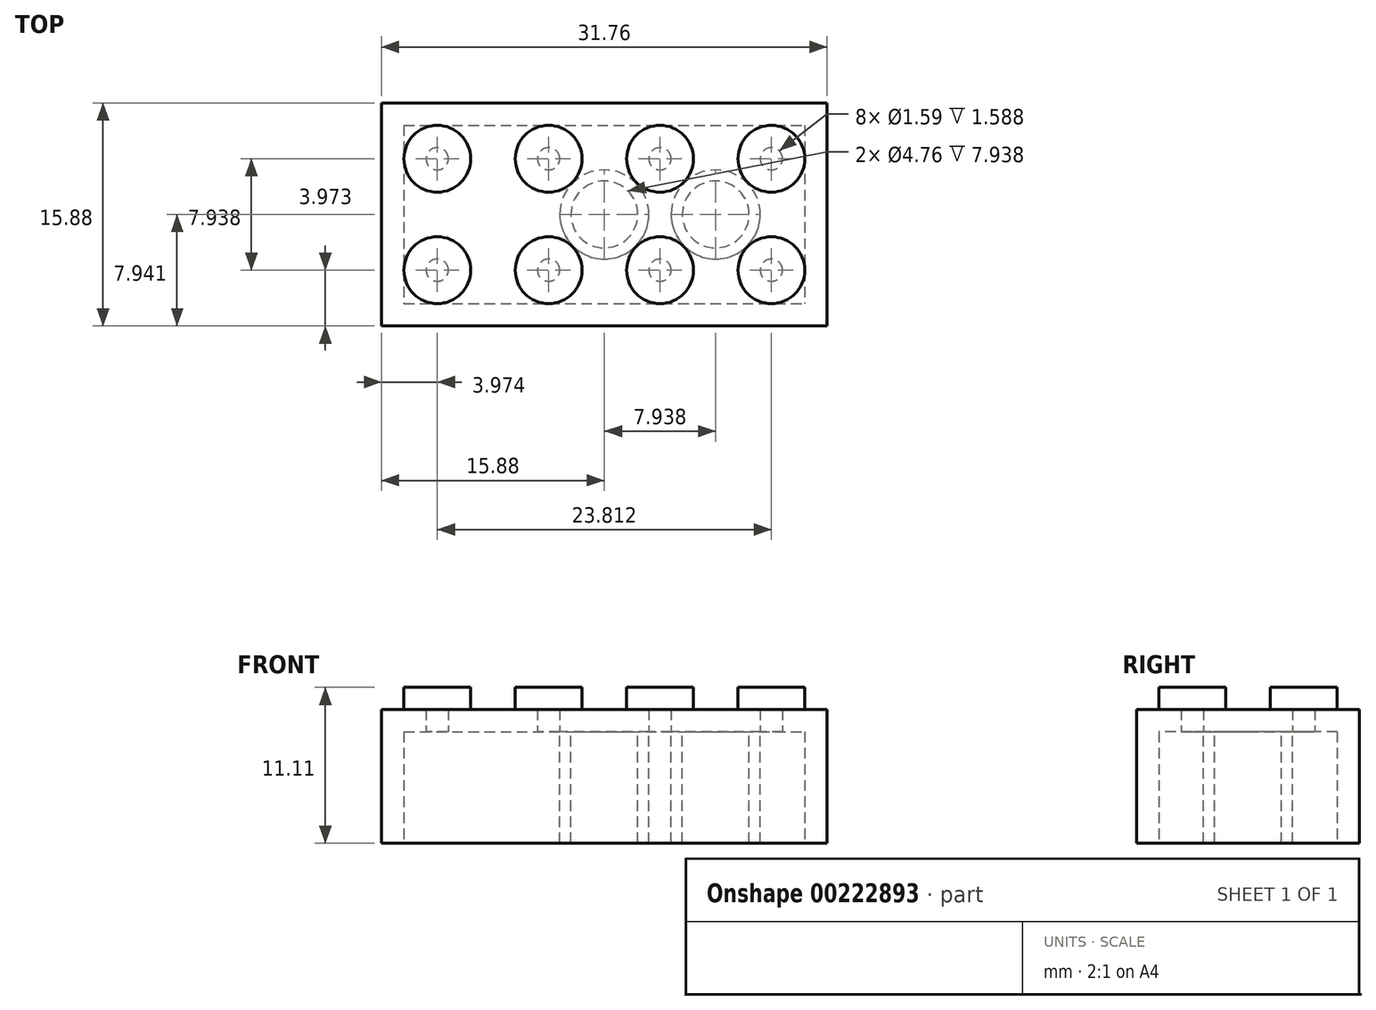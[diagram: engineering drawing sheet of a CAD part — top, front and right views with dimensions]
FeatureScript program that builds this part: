
annotation { "Feature Type Name" : "Feature", "Feature Type Description" : "" }
export const myFeature = defineFeature(function(context is Context, id is Id, definition is map)
    precondition{}
    {
        {
            var Q0;
            Q0=qCreatedBy(makeId("Top.planeOp"),FACE);
            var sketch = newSketch(context, id + "F0", { "sketchPlane" : qUnion([Q0])});
            skLineSegment(sketch, "E0.bottom", {"start": v(-15.88, 3.97) * mm, "end": v(15.87, 3.97) * mm});
            skLineSegment(sketch, "E0.top", {"start": v(-15.88, -11.9) * mm, "end": v(15.87, -11.9) * mm});
            skLineSegment(sketch, "E0.left", {"start": v(-15.88, 3.97) * mm, "end": v(-15.88, -11.9) * mm});
            skLineSegment(sketch, "E0.right", {"start": v(15.88, 3.97) * mm, "end": v(15.88, -11.9) * mm});
            skCircle(sketch, "E1", {"center": v(-11.9, 0) * mm, "radius": 2.38 * mm});
            skCircle(sketch, "E2.0.1.0", {"center": v(-11.9, -7.94) * mm, "radius": 2.38 * mm});
            skCircle(sketch, "E2.1.0.0", {"center": v(-3.97, 0) * mm, "radius": 2.38 * mm});
            skCircle(sketch, "E2.1.1.0", {"center": v(-3.97, -7.94) * mm, "radius": 2.38 * mm});
            skCircle(sketch, "E2.2.0.0", {"center": v(3.97, 0) * mm, "radius": 2.38 * mm});
            skCircle(sketch, "E2.2.1.0", {"center": v(3.97, -7.94) * mm, "radius": 2.38 * mm});
            skCircle(sketch, "E2.3.0.0", {"center": v(11.9, 0) * mm, "radius": 2.38 * mm});
            skCircle(sketch, "E2.3.1.0", {"center": v(11.9, -7.94) * mm, "radius": 2.38 * mm});
            skLineSegment(sketch, "E2.direction1", {"start": v(-11.9, 0) * mm, "end": v(-3.97, 0) * mm, "construction": true});
            skLineSegment(sketch, "E2.direction2", {"start": v(-11.9, 0) * mm, "end": v(-11.9, -7.94) * mm, "construction": true});
            skSolve(sketch);
        }
        {
            var Q0;
            Q0=makeQuery(id+"F0.imprint","IMPRINT",FACE,{"disambiguationData":[TD([[makeQuery(id+"F0.imprint","IMPRINT",EDGE,{"derivedFrom":sQuery(id+"F0.wireOp",EDGE,"E0.bottom")}),-1.0]])]});
            extrude(context, id + "F1", {"entities" : qUnion([Q0]), "depth" : 9.52 * mm});
        }
        {
            var Q0;
            Q0=makeQuery(id+"F0.imprint","IMPRINT",FACE,{"disambiguationData":[TD([[makeQuery(id+"F0.imprint","IMPRINT",EDGE,{"derivedFrom":sQuery(id+"F0.wireOp",EDGE,"E1")}),1.0]])]});
            var Q1;
            Q1=makeQuery(id+"F0.imprint","IMPRINT",FACE,{"disambiguationData":[TD([[makeQuery(id+"F0.imprint","IMPRINT",EDGE,{"derivedFrom":sQuery(id+"F0.wireOp",EDGE,"E2.0.1.0")}),1.0]])]});
            var Q2;
            Q2=makeQuery(id+"F0.imprint","IMPRINT",FACE,{"disambiguationData":[TD([[makeQuery(id+"F0.imprint","IMPRINT",EDGE,{"derivedFrom":sQuery(id+"F0.wireOp",EDGE,"E2.1.1.0")}),1.0]])]});
            var Q3;
            Q3=makeQuery(id+"F0.imprint","IMPRINT",FACE,{"disambiguationData":[TD([[makeQuery(id+"F0.imprint","IMPRINT",EDGE,{"derivedFrom":sQuery(id+"F0.wireOp",EDGE,"E2.1.0.0")}),1.0]])]});
            var Q4;
            Q4=makeQuery(id+"F0.imprint","IMPRINT",FACE,{"disambiguationData":[TD([[makeQuery(id+"F0.imprint","IMPRINT",EDGE,{"derivedFrom":sQuery(id+"F0.wireOp",EDGE,"E2.2.0.0")}),1.0]])]});
            var Q5;
            Q5=makeQuery(id+"F0.imprint","IMPRINT",FACE,{"disambiguationData":[TD([[makeQuery(id+"F0.imprint","IMPRINT",EDGE,{"derivedFrom":sQuery(id+"F0.wireOp",EDGE,"E2.2.1.0")}),1.0]])]});
            var Q6;
            Q6=makeQuery(id+"F0.imprint","IMPRINT",FACE,{"disambiguationData":[TD([[makeQuery(id+"F0.imprint","IMPRINT",EDGE,{"derivedFrom":sQuery(id+"F0.wireOp",EDGE,"E2.3.1.0")}),1.0]])]});
            var Q7;
            Q7=makeQuery(id+"F0.imprint","IMPRINT",FACE,{"disambiguationData":[TD([[makeQuery(id+"F0.imprint","IMPRINT",EDGE,{"derivedFrom":sQuery(id+"F0.wireOp",EDGE,"E2.3.0.0")}),1.0]])]});
            extrude(context, id + "F2", {"entities" : qUnion([Q0, Q1, Q2, Q3, Q4, Q5, Q6, Q7]), "operationType" : NewBodyOperationType.ADD, "depth" : 11.1 * mm});
        }
        {
            var Q0;
            {var subQ0=sQuery(id+"F0.wireOp",EDGE,"8b71ed98-f0e1-4300-85cb-82ad82c44b3e0.MirrorC");var subQ1=sQuery(id+"F0.wireOp",EDGE,"E1");Q0=makeQuery(id+"F2.boolean.opBoolean","MERGE",FACE,{"derivedFrom":[makeQuery(id+"F1.opExtrude","CAP_FACE",FACE,{"disambiguationData":[OSD([sQuery(id+"F0.wireOp",EDGE,"E0.bottom"),sQuery(id+"F0.wireOp",EDGE,"E0.top"),sQuery(id+"F0.wireOp",EDGE,"E0.left"),sQuery(id+"F0.wireOp",EDGE,"E0.right"),subQ1,subQ0])],"isStart":true}),makeQuery(id+"F2.opExtrude","CAP_FACE",FACE,{"disambiguationData":[OSD([subQ1])],"isStart":true}),makeQuery(id+"F2.opExtrude","CAP_FACE",FACE,{"disambiguationData":[OSD([subQ0])],"isStart":true})]});}
            shell(context, id + "F3", {"entities" : qUnion([Q0]), "thickness" : 1.59 * mm});
        }
        {
            var Q0;
            Q0=makeQuery(id+"F3.opShell","OFFSET_FACE",FACE,{"disambiguationData":[OSD([sQuery(id+"F0.wireOp",EDGE,"E0.bottom"),sQuery(id+"F0.wireOp",EDGE,"E0.top"),sQuery(id+"F0.wireOp",EDGE,"E0.left"),sQuery(id+"F0.wireOp",EDGE,"E0.right"),sQuery(id+"F0.wireOp",EDGE,"E1"),sQuery(id+"F0.wireOp",EDGE,"E2.0.1.0"),sQuery(id+"F0.wireOp",EDGE,"E2.1.0.0"),sQuery(id+"F0.wireOp",EDGE,"E2.1.1.0"),sQuery(id+"F0.wireOp",EDGE,"E2.2.0.0"),sQuery(id+"F0.wireOp",EDGE,"E2.2.1.0"),sQuery(id+"F0.wireOp",EDGE,"E2.3.0.0"),sQuery(id+"F0.wireOp",EDGE,"E2.3.1.0")])]});
            var sketch = newSketch(context, id + "F4", { "sketchPlane" : qUnion([Q0])});
            skLineSegment(sketch, "E3", {"start": v(-11.9, 7.94) * mm, "end": v(-3.97, 0) * mm});
            skCircle(sketch, "E4", {"center": v(-7.94, 3.97) * mm, "radius": 3.18 * mm});
            skCircle(sketch, "E5.0", {"center": v(-7.94, 3.97) * mm, "radius": 2.38 * mm});
            skCircle(sketch, "E6.1.0.0", {"center": v(0, 3.97) * mm, "radius": 3.18 * mm});
            skCircle(sketch, "E6.1.0.1", {"center": v(0, 3.97) * mm, "radius": 2.38 * mm});
            skCircle(sketch, "E6.2.0.0", {"center": v(7.94, 3.97) * mm, "radius": 3.18 * mm});
            skCircle(sketch, "E6.2.0.1", {"center": v(7.94, 3.97) * mm, "radius": 2.38 * mm});
            skLineSegment(sketch, "E6.direction1", {"start": v(-7.94, 3.97) * mm, "end": v(0, 3.97) * mm, "construction": true});
            skSolve(sketch);
        }
        {
            var Q0;
            {var subQ0=sQuery(id+"F4.wireOp",EDGE,"E4");var subQ1=sQuery(id+"F4.wireOp",EDGE,"E3");var subQ2=makeQuery(id+"F4.imprint","INTERSECT",VERTEX,{"disambiguationData":[OD(0.0)],"derivedFrom":[subQ1,subQ0]});Q0=makeQuery(id+"F4.imprint","IMPRINT",FACE,{"disambiguationData":[TD([[makeQuery(id+"F4.imprint","IMPRINT",EDGE,{"disambiguationData":[TD([[subQ2,-1.0]])],"derivedFrom":subQ1}),1.0]])]});}
            var Q1;
            {var subQ0=sQuery(id+"F4.wireOp",EDGE,"E4");var subQ1=sQuery(id+"F4.wireOp",EDGE,"E3");var subQ2=makeQuery(id+"F4.imprint","INTERSECT",VERTEX,{"disambiguationData":[OD(0.0)],"derivedFrom":[subQ1,subQ0]});Q1=makeQuery(id+"F4.imprint","IMPRINT",FACE,{"disambiguationData":[TD([[makeQuery(id+"F4.imprint","IMPRINT",EDGE,{"disambiguationData":[TD([[subQ2,-1.0]])],"derivedFrom":subQ1}),-1.0]])]});}
            var Q2;
            Q2=makeQuery(id+"F4.imprint","IMPRINT",FACE,{"disambiguationData":[TD([[makeQuery(id+"F4.imprint","IMPRINT",EDGE,{"derivedFrom":sQuery(id+"F4.wireOp",EDGE,"E6.1.0.0")}),1.0]])]});
            var Q3;
            Q3=makeQuery(id+"F4.imprint","IMPRINT",FACE,{"disambiguationData":[TD([[makeQuery(id+"F4.imprint","IMPRINT",EDGE,{"derivedFrom":sQuery(id+"F4.wireOp",EDGE,"E6.2.0.0")}),1.0]])]});
            extrude(context, id + "F5", {"entities" : qUnion([Q0, Q1, Q2, Q3]), "operationType" : NewBodyOperationType.ADD, "depth" : 7.94 * mm});
        }
    });
